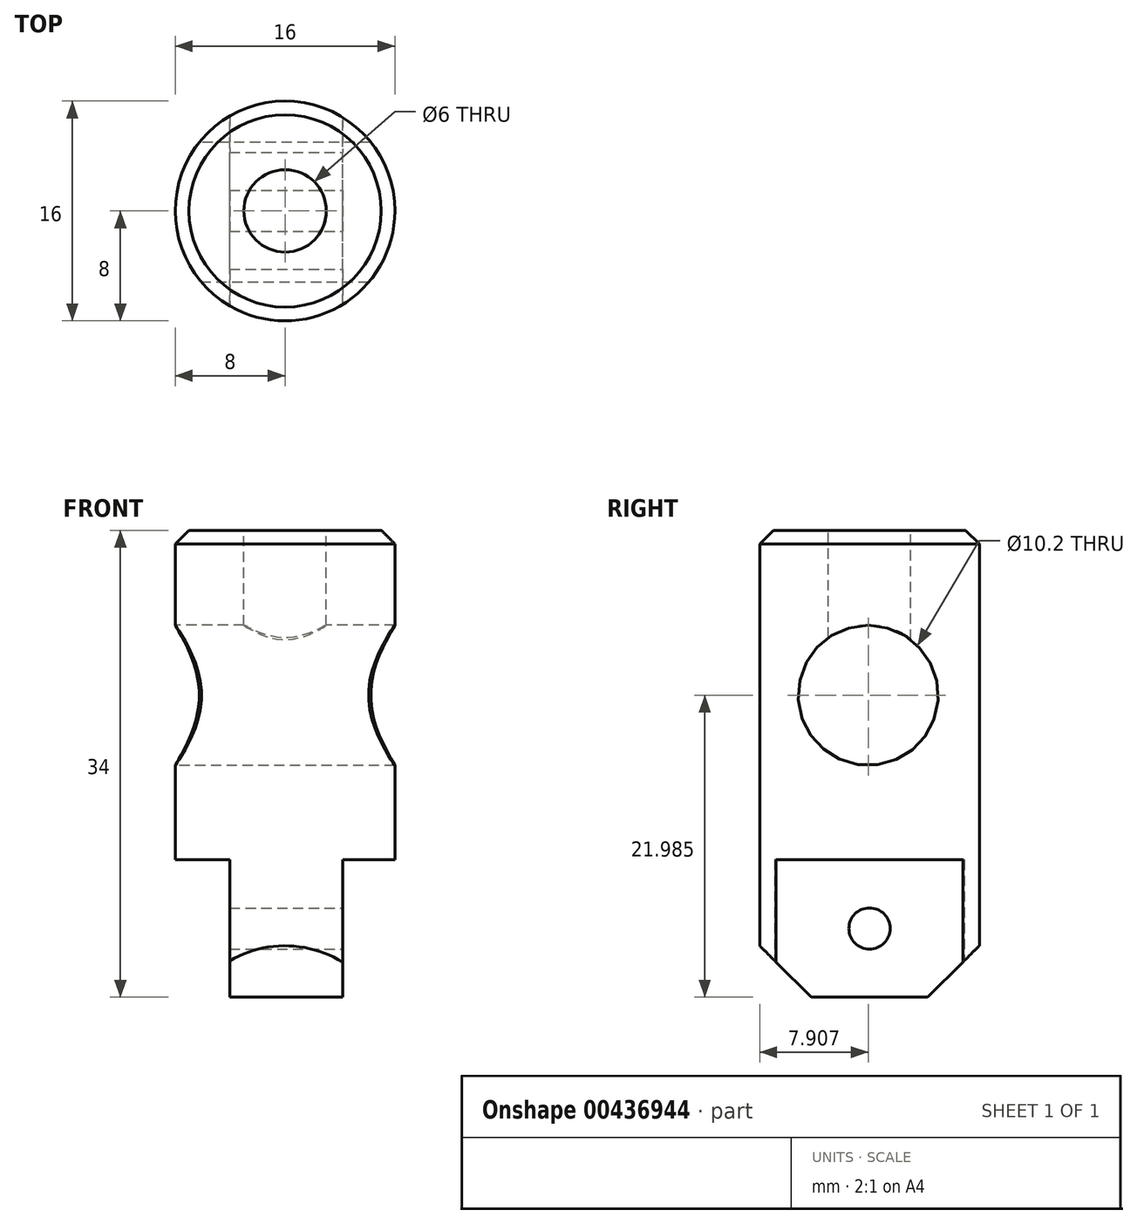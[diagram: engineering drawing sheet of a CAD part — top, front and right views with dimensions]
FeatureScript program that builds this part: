
annotation { "Feature Type Name" : "Feature", "Feature Type Description" : "" }
export const myFeature = defineFeature(function(context is Context, id is Id, definition is map)
    precondition{}
    {
        {
            var Q0;
            Q0=qCreatedBy(makeId("Top.planeOp"),FACE);
            var sketch = newSketch(context, id + "F0", { "sketchPlane" : qUnion([Q0])});
            skCircle(sketch, "E0", {"center": v(0, 0) * mm, "radius": 8 * mm});
            skSolve(sketch);
        }
        {
            var Q0;
            Q0 = qSketchRegion(id + "F0", true);
            extrude(context, id + "F1", {"entities" : qUnion([Q0]), "depth" : 34 * mm});
        }
        {
            var Q0;
            Q0=qCreatedBy(makeId("Right.planeOp"),FACE);
            var sketch = newSketch(context, id + "F2", { "sketchPlane" : qUnion([Q0])});
            skLineSegment(sketch, "E1", {"start": v(-8.06, 34.07) * mm, "end": v(-8.06, 22.07) * mm});
            skLineSegment(sketch, "E2", {"start": v(-8.06, 22.07) * mm, "end": v(8.09, 22.07) * mm});
            skCircle(sketch, "E3", {"center": v(0, 22.07) * mm, "radius": 4.55 * mm});
            skSolve(sketch);
        }
        {
            var Q0;
            Q0 = qSketchRegion(id + "F2", true);
            extrude(context, id + "F3", {"entities" : qUnion([Q0]), "operationType" : NewBodyOperationType.REMOVE, "oppositeDirection" : true, "depth" : 100 * mm});
        }
        {
            var Q0;
            Q0=qCreatedBy(makeId("Right.planeOp"),FACE);
            var sketch = newSketch(context, id + "F4", { "sketchPlane" : qUnion([Q0])});
            skLineSegment(sketch, "E4", {"start": v(-8.06, 33.99) * mm, "end": v(-8.06, 21.99) * mm});
            skLineSegment(sketch, "E5", {"start": v(-8.06, 21.99) * mm, "end": v(7.87, 21.99) * mm});
            skCircle(sketch, "E6", {"center": v(-0.1, 21.99) * mm, "radius": 5.1 * mm});
            skSolve(sketch);
        }
        {
            var Q0;
            Q0 = qSketchRegion(id + "F4", true);
            extrude(context, id + "F5", {"entities" : qUnion([Q0]), "operationType" : NewBodyOperationType.REMOVE, "endBound" : BoundingType.THROUGH_ALL, "depth" : 100 * mm, "hasSecondDirection" : true, "secondDirectionOppositeDirection" : true, "secondDirectionDepth" : 50 * mm});
        }
        {
            var Q0;
            Q0=makeQuery(id+"F1.opExtrude","CAP_FACE",FACE,{"disambiguationData":[OSD([sQuery(id+"F0.wireOp",EDGE,"E0")])],"isStart":false});
            var sketch = newSketch(context, id + "F6", { "sketchPlane" : qUnion([Q0])});
            skCircle(sketch, "E7", {"center": v(0, 0) * mm, "radius": 7 * mm});
            skSolve(sketch);
        }
        {
            var Q0;
            Q0=makeQuery(id+"F1.opExtrude","CAP_FACE",FACE,{"disambiguationData":[OSD([sQuery(id+"F0.wireOp",EDGE,"E0")])],"isStart":false});
            chamfer(context, id + "F7", {"entities" : qUnion([Q0]), "chamferType" : ChamferType.OFFSET_ANGLE, "width" : 1 * mm, "oppositeDirection" : false, "angle" : 45 * degree, "tangentPropagation" : true});
        }
        {
            var Q0;
            Q0=qCreatedBy(makeId("Right.planeOp"),FACE);
            var sketch = newSketch(context, id + "F8", { "sketchPlane" : qUnion([Q0])});
            skPoint(sketch, "E8.end.orphan", {"position": v(-6.03, 5) * mm});
            skPoint(sketch, "E8.start.orphan", {"position": v(-6.03, 0) * mm});
            skCircle(sketch, "E9", {"center": v(0, 5) * mm, "radius": 1.5 * mm});
            skPoint(sketch, "E10.end.orphan", {"position": v(-8.07, 5) * mm});
            skPoint(sketch, "E10.start.orphan", {"position": v(-8.07, 0) * mm});
            skPoint(sketch, "E11.end.orphan", {"position": v(8.06, 5) * mm});
            skPoint(sketch, "E11.start.orphan", {"position": v(8.06, 0) * mm});
            skSolve(sketch);
        }
        {
            var Q0;
            Q0 = qSketchRegion(id + "F8", true);
            extrude(context, id + "F9", {"entities" : qUnion([Q0]), "operationType" : NewBodyOperationType.REMOVE, "oppositeDirection" : true, "depth" : 50 * mm, "hasSecondDirection" : true, "secondDirectionOppositeDirection" : false, "secondDirectionDepth" : 50 * mm});
        }
        {
            var Q0;
            Q0=qCreatedBy(makeId("Right.planeOp"),FACE);
            var sketch = newSketch(context, id + "F10", { "sketchPlane" : qUnion([Q0])});
            skLineSegment(sketch, "E12", {"start": v(-8.56, 0) * mm, "end": v(-8.56, 4.31) * mm});
            skLineSegment(sketch, "E13", {"start": v(8.56, 0) * mm, "end": v(8.56, 4.31) * mm});
            skLineSegment(sketch, "E14", {"start": v(0, 0) * mm, "end": v(-4.25, 0) * mm});
            skPoint(sketch, "E15.start.orphan", {"position": v(0.2, 0) * mm});
            skLineSegment(sketch, "E16", {"start": v(0, 0) * mm, "end": v(0.2, 0) * mm});
            skLineSegment(sketch, "E17", {"start": v(0, 0) * mm, "end": v(4.25, 0) * mm});
            skPoint(sketch, "E17.endSnap0", {"position": v(0.1, 0) * mm});
            skLineSegment(sketch, "E18", {"start": v(-4.25, 0) * mm, "end": v(-8.56, 0) * mm});
            skLineSegment(sketch, "E19", {"start": v(4.25, 0) * mm, "end": v(8.56, 0) * mm});
            skLineSegment(sketch, "E20", {"start": v(8.56, 4.31) * mm, "end": v(4.25, 0) * mm});
            skLineSegment(sketch, "E21", {"start": v(-4.25, 0) * mm, "end": v(-8.56, 4.31) * mm});
            skSolve(sketch);
        }
        {
            var Q0;
            Q0 = qSketchRegion(id + "F10", true);
            extrude(context, id + "F11", {"entities" : qUnion([Q0]), "operationType" : NewBodyOperationType.REMOVE, "oppositeDirection" : true, "depth" : 50 * mm, "hasSecondDirection" : true, "secondDirectionOppositeDirection" : false, "secondDirectionDepth" : 50 * mm});
        }
        {
            var Q0;
            Q0=makeQuery(id+"F6.imprint","IMPRINT",FACE,{"disambiguationData":[TD([[makeQuery(id+"F6.imprint","IMPRINT",EDGE,{"derivedFrom":sQuery(id+"F6.wireOp",EDGE,"E7")}),1.0]])]});
            var sketch = newSketch(context, id + "F12", { "sketchPlane" : qUnion([Q0])});
            skCircle(sketch, "E22", {"center": v(0, 0) * mm, "radius": 3 * mm});
            skSolve(sketch);
        }
        {
            var Q0;
            Q0 = qSketchRegion(id + "F12", true);
            extrude(context, id + "F13", {"entities" : qUnion([Q0]), "operationType" : NewBodyOperationType.REMOVE, "oppositeDirection" : true, "depth" : 12 * mm});
        }
        {
            var Q0;
            Q0=makeQuery(id+"F6.imprint","IMPRINT",FACE,{"disambiguationData":[TD([[makeQuery(id+"F6.imprint","IMPRINT",EDGE,{"derivedFrom":sQuery(id+"F6.wireOp",EDGE,"E7")}),1.0]])]});
            var sketch = newSketch(context, id + "F14", { "sketchPlane" : qUnion([Q0])});
            skLineSegment(sketch, "E23", {"start": v(0, 0) * mm, "end": v(-4.25, 0) * mm});
            skLineSegment(sketch, "E24", {"start": v(0, 0) * mm, "end": v(4.25, 0) * mm});
            skLineSegment(sketch, "E25", {"start": v(4.25, 0) * mm, "end": v(4.25, -8.9) * mm});
            skLineSegment(sketch, "E26", {"start": v(4.25, -8.9) * mm, "end": v(4.25, 8.16) * mm});
            skLineSegment(sketch, "E27", {"start": v(4.25, 8.16) * mm, "end": v(9.46, 8.16) * mm});
            skLineSegment(sketch, "E28", {"start": v(9.46, 8.16) * mm, "end": v(9.46, -8.9) * mm});
            skLineSegment(sketch, "E29", {"start": v(9.46, -8.9) * mm, "end": v(4.25, -8.9) * mm});
            skLineSegment(sketch, "E30", {"start": v(-4.25, 0) * mm, "end": v(-4.25, -8.9) * mm});
            skLineSegment(sketch, "E31", {"start": v(-4.25, 0) * mm, "end": v(-4.25, 8.1) * mm});
            skLineSegment(sketch, "E32", {"start": v(-4.25, 8.1) * mm, "end": v(-12.22, 8.1) * mm});
            skLineSegment(sketch, "E33", {"start": v(-12.22, 8.1) * mm, "end": v(-12.22, -9.06) * mm});
            skLineSegment(sketch, "E34", {"start": v(-12.22, -9.06) * mm, "end": v(-4.25, -8.9) * mm});
            skSolve(sketch);
        }
        {
            var Q0;
            Q0 = qSketchRegion(id + "F14", true);
            extrude(context, id + "F15", {"entities" : qUnion([Q0]), "operationType" : NewBodyOperationType.REMOVE, "depth" : 10 * mm});
        }
        {
            var Q0;
            Q0=qCreatedBy(makeId("Top.planeOp"),FACE);
            var sketch = newSketch(context, id + "F16", { "sketchPlane" : qUnion([Q0])});
            skLineSegment(sketch, "E35", {"start": v(-7.78, 0) * mm, "end": v(-4.03, 0) * mm});
            skLineSegment(sketch, "E36", {"start": v(8.38, 0) * mm, "end": v(4.63, 0) * mm});
            skLineSegment(sketch, "E37", {"start": v(4.63, 0) * mm, "end": v(4.19, 0) * mm});
            skLineSegment(sketch, "E38.bottom", {"start": v(-4.03, -8.19) * mm, "end": v(-8.8, -8.19) * mm});
            skLineSegment(sketch, "E38.top", {"start": v(-4.03, 8.8) * mm, "end": v(-8.8, 8.8) * mm});
            skLineSegment(sketch, "E38.left", {"start": v(-4.03, -8.19) * mm, "end": v(-4.03, 8.8) * mm});
            skLineSegment(sketch, "E38.right", {"start": v(-8.8, -8.19) * mm, "end": v(-8.8, 8.8) * mm});
            skLineSegment(sketch, "E39.bottom", {"start": v(4.19, -9.24) * mm, "end": v(9.38, -9.24) * mm});
            skLineSegment(sketch, "E39.top", {"start": v(4.19, 8.8) * mm, "end": v(9.38, 8.8) * mm});
            skLineSegment(sketch, "E39.left", {"start": v(4.19, -9.24) * mm, "end": v(4.19, 8.8) * mm});
            skLineSegment(sketch, "E39.right", {"start": v(9.38, -9.24) * mm, "end": v(9.38, 8.8) * mm});
            skSolve(sketch);
        }
        {
            var Q0;
            Q0 = qSketchRegion(id + "F16", true);
            extrude(context, id + "F17", {"entities" : qUnion([Q0]), "operationType" : NewBodyOperationType.REMOVE, "depth" : 10 * mm});
        }
    });
